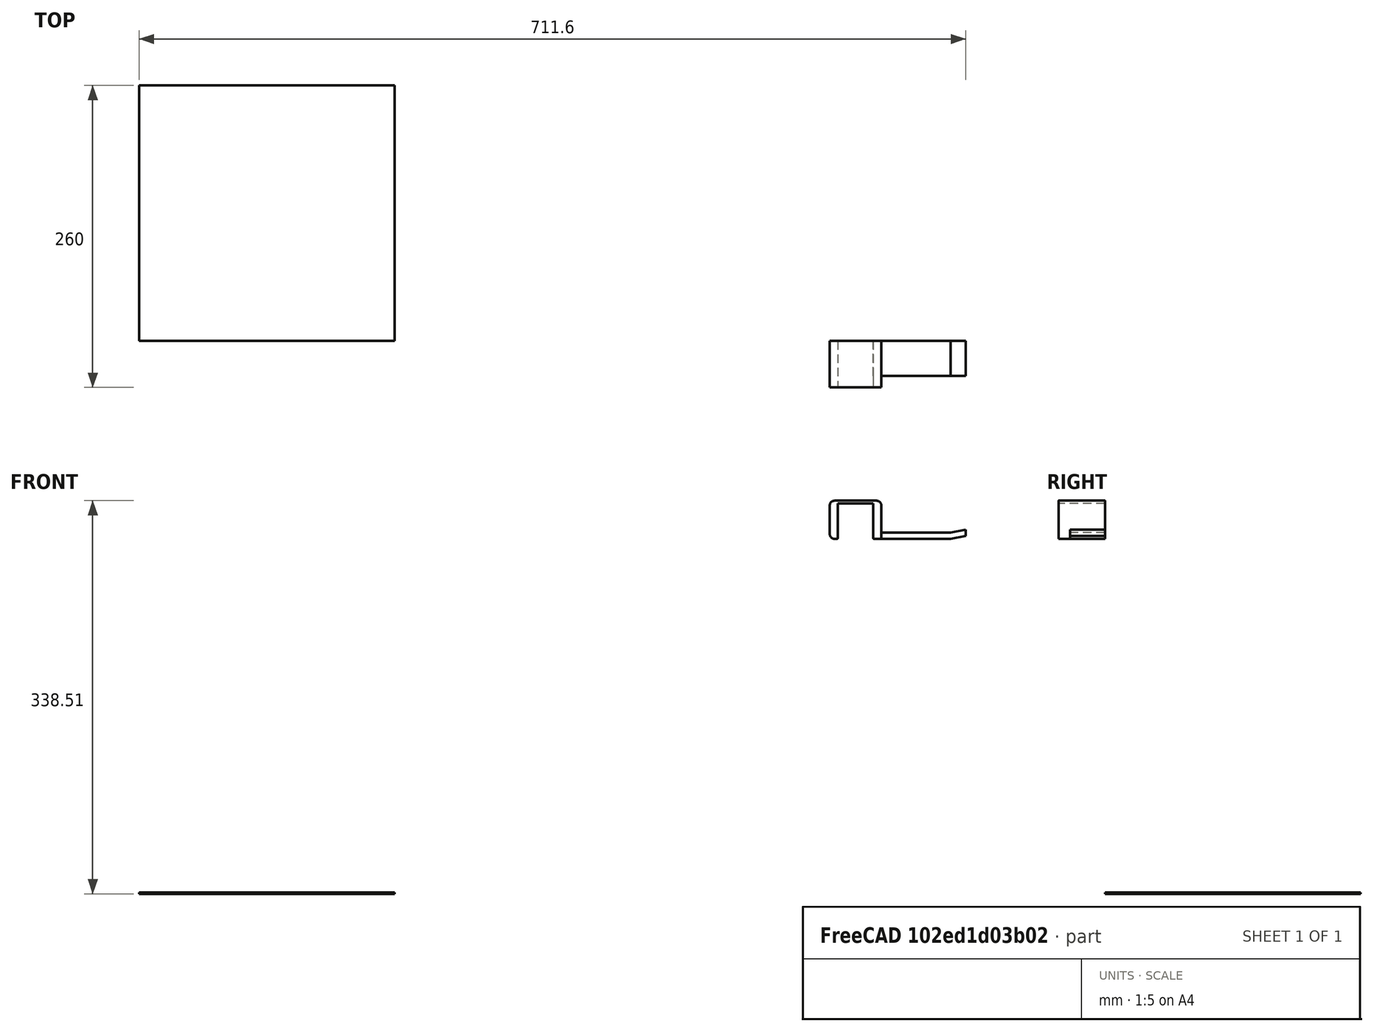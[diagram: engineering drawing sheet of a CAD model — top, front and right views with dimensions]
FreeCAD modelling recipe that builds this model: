
FCSTD DOCUMENT  (FreeCAD 0.20R29603 (Git))
Label: Spool Holder
License: All rights reserved
LicenseURL: http://en.wikipedia.org/wiki/All_rights_reserved
objects: PartDesign::Pad×6, PartDesign::Fillet×4, Sketcher::SketchObject×3, Mesh::Feature×2, PartDesign::Pocket×2, Part::Box×1, PartDesign::Body×1
note: 29 computed .brp shape members not serialized (recipe doc carries the construction recipe); baked Part::Feature solids carry a one-line shape summary decoded from their .brp

FEATURE [Mesh::Feature] Rook180_Turned___Top_Frame_Extender_227  label="Rook180_Turned - Top_Frame_Extender-227"
  Placement = pos=(763.675,149.306,165.769) rot=(0,0,1;4.71239rad)
FEATURE [Mesh::Feature] T_TOP_Right_Rear_Frame__V1_1  label="T_TOP_Right_Rear_Frame _V1_1"
  Placement = pos=(631.895,0,402.052) rot=(0,1,0;3.14159rad)
FEATURE [Sketcher::SketchObject] Sketch
  FullyConstrained = false
  Placement = pos=(0,0,0) rot=(1,0,0;1.5708rad)
  sketch-geometry (8):
    g0: LineSegment StartX=601.65 StartY=335.956 StartZ=0 EndX=631.977 EndY=335.956 EndZ=0
    g1: LineSegment StartX=631.977 StartY=335.956 StartZ=0 EndX=631.977 EndY=305.598 EndZ=0
    g2: LineSegment StartX=601.65 StartY=335.956 StartZ=0 EndX=601.65 EndY=305.598 EndZ=0
    g3: LineSegment StartX=601.65 StartY=305.598 StartZ=0 EndX=599.65 EndY=305.598 EndZ=0
    g4: LineSegment StartX=599.65 StartY=305.598 StartZ=0 EndX=599.65 EndY=338.508 EndZ=0
    g5: LineSegment StartX=631.977 StartY=305.598 StartZ=0 EndX=633.949 EndY=305.598 EndZ=0
    g6: LineSegment StartX=633.949 StartY=305.598 StartZ=0 EndX=633.949 EndY=338.508 EndZ=0
    g7: LineSegment StartX=599.65 StartY=338.508 StartZ=0 EndX=633.949 EndY=338.508 EndZ=0
  constraints (18):
    c: Coincident(g0,g1)
    c: Horizontal(g0)
    c: Vertical(g1)
    c: Coincident(g2,g0)
    c: Vertical(g2)
    c: Horizontal(g2,g1)
    c: Coincident(g3,g2)
    c: Horizontal(g3)
    c: DistanceX(g3,g3) = 2
    c: Coincident(g4,g3)
    c: Vertical(g4)
    c: Coincident(g5,g1)
    c: Horizontal(g5)
    c: Coincident(g6,g5)
    c: Vertical(g6)
    c: Horizontal(g6,g4)
    c: Coincident(g7,g4)
    c: Coincident(g7,g6)
FEATURE [PartDesign::Pad] Pad
  Direction = (0,-1,0)
  Length = 40
  Length2 = 10
  Placement = pos=(0,0,0) rot=(1,0,0;1.5708rad)
  Profile = -> Sketch
  ReferenceAxis = -> Sketch [N_Axis]
  Type = 0
FEATURE [Sketcher::SketchObject] Sketch001
  AttachmentOffset = pos=(0,-3,630) rot=(0,0,1;0rad)
  FullyConstrained = false
  MapMode = 5
  Placement = pos=(630,-1.406e-13,-3) rot=(0.57735,0.57735,0.57735;2.0944rad)
  Support = -> [YZ_Plane]
  sketch-geometry (4):
    g0: LineSegment StartX=-30.0017 StartY=308.606 StartZ=0 EndX=-0.00171812 EndY=308.606 EndZ=0
    g1: LineSegment StartX=-0.00171812 StartY=308.606 StartZ=0 EndX=-0.00171812 EndY=313.884 EndZ=0
    g2: LineSegment StartX=-0.00171812 StartY=313.884 StartZ=0 EndX=-30.0017 EndY=313.884 EndZ=0
    g3: LineSegment StartX=-30.0017 StartY=313.884 StartZ=0 EndX=-30.0017 EndY=308.606 EndZ=0
  constraints (9):
    c: Coincident(g0,g1)
    c: Coincident(g1,g2)
    c: Coincident(g2,g3)
    c: Coincident(g3,g0)
    c: Horizontal(g0)
    c: Horizontal(g2)
    c: Vertical(g1)
    c: Vertical(g3)
    c: Distance(g0) = 30
FEATURE [PartDesign::Pad] Pad001
  BaseFeature = -> Pad
  Direction = (1,-2e-16,3e-16)
  Length = 105
  Length2 = 10
  Placement = pos=(0,0,0) rot=(1,0,0;1.5708rad)
  Profile = -> Sketch001
  ReferenceAxis = -> Sketch001 [N_Axis]
  Type = 0
FEATURE [PartDesign::Pocket] Pocket
  BaseFeature = -> Pad001
  Direction = (2e-16,1,-2e-16)
  Length = 5
  Length2 = 5
  Placement = pos=(0,0,0) rot=(1,0,0;1.5708rad)
  Profile = -> Pad001 [Face10]
  Type = 1
FEATURE [Part::Box] Box  label="Cube"
  AttacherType = Attacher::AttachEngine3D
  Height = 1
  Length = 220
  Width = 220
FEATURE [PartDesign::Pad] Pad002
  BaseFeature = -> Pocket
  Direction = (-1,0,0)
  Length = 5
  Length2 = 10
  Placement = pos=(0,0,0) rot=(1,0,0;1.5708rad)
  Profile = -> Pocket [Face12]
  Type = 0
FEATURE [PartDesign::Pad] Pad003
  BaseFeature = -> Pad002
  Direction = (1,0,0)
  Length = 5
  Length2 = 10
  Placement = pos=(0,0,0) rot=(1,0,0;1.5708rad)
  Profile = -> Pad002 [Face10]
  Type = 0
FEATURE [PartDesign::Pad] Pad004
  BaseFeature = -> Pad003
  Direction = (1,0,0.7)
  Length = 10
  Length2 = 10
  Placement = pos=(0,0,0) rot=(1,0,0;1.5708rad)
  Profile = -> Pad003 [Face25]
  Type = 0
  UseCustomVector = true
FEATURE [PartDesign::Fillet] Fillet
  Base = -> Pad004 [Edge47,Edge52]
  BaseFeature = -> Pad004
  Placement = pos=(0,0,0) rot=(1,0,0;1.5708rad)
  Radius = 4
  SupportTransform = false
  UseAllEdges = false
FEATURE [PartDesign::Fillet] Fillet001
  Base = -> Fillet [Edge64]
  BaseFeature = -> Fillet
  Placement = pos=(0,0,0) rot=(1,0,0;1.5708rad)
  Radius = 4
  SupportTransform = false
  UseAllEdges = false
FEATURE [PartDesign::Fillet] Fillet002
  Base = -> Fillet001 [Edge28]
  BaseFeature = -> Fillet001
  Placement = pos=(0,0,0) rot=(1,0,0;1.5708rad)
  Radius = 1
  SupportTransform = false
  UseAllEdges = false
FEATURE [PartDesign::Fillet] Fillet003
  Base = -> Fillet002 [Edge38]
  BaseFeature = -> Fillet002
  Placement = pos=(0,0,0) rot=(1,0,0;1.5708rad)
  Radius = 1
  SupportTransform = false
  UseAllEdges = false
FEATURE [Sketcher::SketchObject] Sketch002
  FullyConstrained = false
  MapMode = 5
  Placement = pos=(0,0,0) rot=(1,0,0;1.5708rad)
  Support = -> [XZ_Plane]
  sketch-geometry (4):
    g0: LineSegment StartX=773.524 StartY=337.963 StartZ=0 EndX=698.603 EndY=337.963 EndZ=0
    g1: LineSegment StartX=698.603 StartY=337.963 StartZ=0 EndX=698.603 EndY=279.58 EndZ=0
    g2: LineSegment StartX=698.603 StartY=279.58 StartZ=0 EndX=773.524 EndY=279.58 EndZ=0
    g3: LineSegment StartX=773.524 StartY=279.58 StartZ=0 EndX=773.524 EndY=337.963 EndZ=0
  constraints (8):
    c: Coincident(g0,g1)
    c: Coincident(g1,g2)
    c: Coincident(g2,g3)
    c: Coincident(g3,g0)
    c: Horizontal(g0)
    c: Horizontal(g2)
    c: Vertical(g1)
    c: Vertical(g3)
FEATURE [PartDesign::Pocket] Pocket001
  BaseFeature = -> Fillet003
  Direction = (0,1,-2e-16)
  Length = 36
  Length2 = 5
  Placement = pos=(0,0,0) rot=(1,0,0;1.5708rad)
  Profile = -> Sketch002
  ReferenceAxis = -> Sketch002 [N_Axis]
  Reversed = true
  Type = 0
FEATURE [PartDesign::Pad] Pad005
  BaseFeature = -> Pocket001
  Direction = (1,0,0.2)
  Length = 13
  Length2 = 10
  Placement = pos=(0,0,0) rot=(1,0,0;1.5708rad)
  Profile = -> Pocket001 [Face32]
  Type = 0
  UseCustomVector = true
FEATURE [PartDesign::Body] Body
  Group = -> [Sketch,Pad,Sketch001,Pad001,Pocket,Pad002,Pad003,Pad004,Fillet,Fillet001,Fillet002,Fillet003,Sketch002,Pocket001,Pad005]
  Origin = -> Origin
  Tip = -> Pad005
